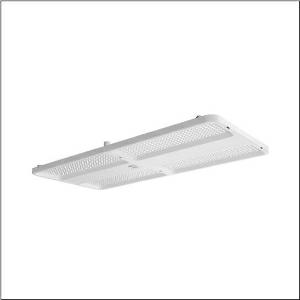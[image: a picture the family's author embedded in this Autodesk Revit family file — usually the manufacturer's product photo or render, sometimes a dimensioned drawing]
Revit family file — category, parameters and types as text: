
# Revit family: highbay_21_maxi_52hn11db4qda01
name_source: partatom
category: Lighting Fixtures
units: mm (PartAtom-declared; Revit-internal decimal feet)

## family parameters
Cut with Voids When Loaded = No
Host = Face
Light Source = No
Part Type = Normal
Room Calculation Point = No
Round Connector Dimension = Use Diameter
Shared = No

## types (1)
- --- (1 x LED, 38000 lm, 198.2 W, 4000K)
    Apparent Load = 198 VA
    CIE Flux Codes = 89 97 99 100 100
    Color Rendering = 80
    Color Temperature = 4000K
    Default Elevation = 1800 mm
    Description = high bay luminaire Highbay 21 maxi; direct symmetric narrow distribution, light control with lens of PMMA; UGR ≤ 19 (X = 4H | Y = 8H | S = 0.25H | reflection values 70/50/20); luminous flux: 38.000lm; light colour: 840, colour temperature: 4000K, MacAdam ≤ 3 SDCM (initial), colour rendering: CRI > 80; luminous efficacy: 191,7lm/W; rated service life: 75.000h (L80/B50) at AT= ta max; control: Bluetooth® Mesh; for wireless networking: Node multi-sensor luminaire for setting up a local control solution without a higher-level application controller, intelligence completely integrated into the luminaire; with auto-swarm function: leading lighting creates safety. The function is already active without any „out-of-the-box“ commissioning; commissioning is not necessary thanks to „out-of-the-box“ functions: basic functions (presence lighting, follow-up times, fading times, etc.) are already preset at the factory; no control line such as DALI between the Node multi-sensor luminaires and Nodes is required, wireless integration of other Node luminaires and Node multi-sensor luminaires into the network is possible; number of Node multi-sensor luminaires in the project can be expanded as required, network sizes > 300 Nodes can be realized; can also be connected to lighting or building automation via various gateways upon request; integrated DALI2 ECG provides luminaire data (according to IEC62386, Part 251), energy data (Part 252), and monitoring and analytics data (Part 253) to higher-level systems for further processing; luminaire with PIR sensor (passive-infrared); with light sensor; luminaire connection: terminal, 5-pole, max. 2.5mm² (cable entry for one cable, Ø 8.5..16mm); mains connection: 230..240V, AC 50/60Hz; connected load: 198,2W; protection rating (complete): IP65; insulation class (complete): insulation class I (protective earthing); protection symbol: D; certification: CE, ENEC, VDE, UKCA; internal wiring halogen-free; luminaire corresponds to IFS (International Featured Standards) requirements for safety and quality in the food industry; LABS conformity tested according to VDMA 24364:2018-05; housing frame of high-performance plastic PA6, matt traffic white (RAL 9016); cover of PMMA; dimension (LxWxH): 946 x 442 x 72mm; permissible operating ambient temperature: -20..+40°C (reducing of maximum allowable ambient temperature of 5°C with ceiling mounting); packaging unit: 1 piece; (delivery without accessories; please order mounting accessories separately)
    Height = 72 mm  [stored 0.23622 ft]
    Lamp = 1 x LED
    Lamp Light Flux = 38000 lm
    Lamp Power = 198.2 W
    Lamp count = 1
    Length = 946 mm
    Luminous efficacy = 192 lm/W
    Manufacturer = Siteco
    ModVariant = No
    Model = 52HN11DB4QDA01
    Mounting Place = Ceiling
    Mounting Type = Pendant
    Number of Poles = 1
    OnlyDefault = Yes
    Power Factor = 1
    Product Name = Highbay 21 maxi
    Product group = high bay luminaire
    ProductGroupID = 901
    Protection Class = Protection class I
    Protection Degree = IP 65
    RLX_Detail_Level = 1
    RLX_Emergency_Light_Flux = 0 lm
    RLX_Emergency_Type = 0
    RLX_Emergency_Type_DB = No
    RlxData = <blob elided: 128853 chars, md5=b214c0cf>
    Socket = socket
    Standby Power = 0 W
    System Light Flux = 38001 lm
    System Power = 198 W
    Type Comments = factory setting: luminous flux: 100 % | dim-lin: 254 | 918 mA
    Type Image = l_1363267.jpg
    URL = http://relux.com
    VarID = @adj_010527
    Voltage = 0 V
    Weight = 0.00 kg
    Width = 442 mm

note: [stored X ft] marks values corroborated as IEEE doubles in the binary element streams (Revit-internal decimal feet)

## geometry (parser evidence)
native form markers: Blend x4, Sweep x9
no freeform markers — native parametric forms only
